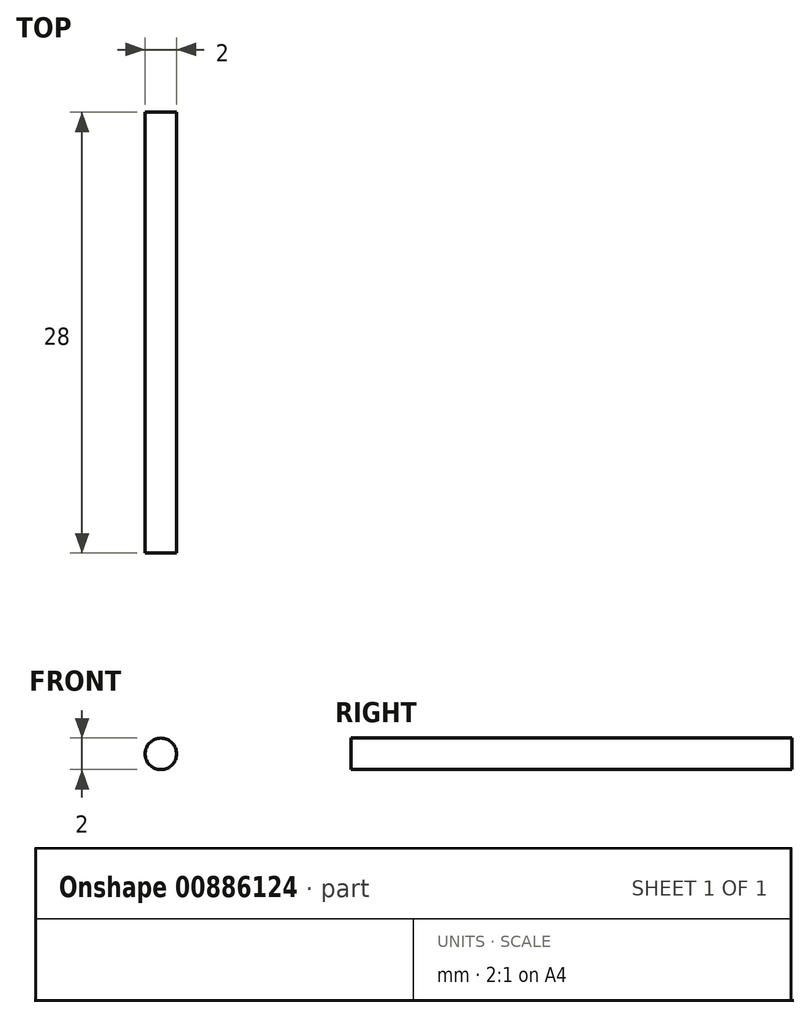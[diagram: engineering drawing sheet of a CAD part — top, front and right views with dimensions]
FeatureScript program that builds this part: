
annotation { "Feature Type Name" : "Feature", "Feature Type Description" : "" }
export const myFeature = defineFeature(function(context is Context, id is Id, definition is map)
    precondition{}
    {
        {
            var Q0;
            Q0=qCreatedBy(makeId("Front.planeOp"),FACE);
            var sketch = newSketch(context, id + "F0", { "sketchPlane" : qUnion([Q0])});
            skCircle(sketch, "E0", {"center": v(0, 0) * mm, "radius": 1 * mm});
            skSolve(sketch);
        }
        {
            var Q0;
            Q0 = qSketchRegion(id + "F0", true);
            extrude(context, id + "F1", {"entities" : qUnion([Q0]), "depth" : 28 * mm, "offsetDistance" : 25 * mm});
        }
    });
